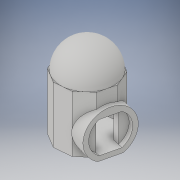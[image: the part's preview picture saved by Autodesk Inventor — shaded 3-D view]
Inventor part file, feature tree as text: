
AUTODESK INVENTOR PART (.ipt)
format: ipt  version: 2017 (Build 210142000, 142)  size: 312,320 bytes
history: native  units: in
note: dims shown in document units (in); Inventor stores cm internally (conversion verified against a paired STEP export)
features: sketch x8, extrude x7, other x4, mirror x1
ambient origin geometry x8: Origin, YZ Plane, XZ Plane, XY Plane, X Axis, Y Axis, Z Axis, Center Point
bodies: Solid1 (feature_tree)
feature tree (20):
  extrude  "bace"  Depth=1.0in TaperAngle=0.0deg
  extrude  "bace wall"  Depth=10.0in TaperAngle=0.0deg
  extrude  "bace cieiling"  Depth=6.6667in
  other  "dome work plane"
  other  "dome"
  extrude  "door frame"  Depth=6.6667in TaperAngle=0.0deg
  extrude  "corridor connection"  Depth=6.6667in
  extrude  "hide sliding doors"  Depth=4.6918in
  extrude  "left door slot"  TaperAngle=90.0deg  [1 undecoded]
  other  "door slot mirror"
  mirror  "Mirror1"
  other  "terminal connection parrale to door workplane"
  sketch  "Sketch1"  dims[d0=11.3835in d1=1.0in d2=0.0in]
  sketch  "Sketch2"  dims[d4=1.0in d5=10.0in d6=0.0in]
  sketch  "Sketch3"  dims[d8=1.0in d9=0.0in d14=6.6667in d15=4.0in]
  sketch  "Sketch7"  dims[d16=2.0in d17=6.6667in d18=1.6875in d19=0.0in]
  sketch  "Sketch8"  dims[d20=1.0in d21=0.0in d22=0.25in d23=0.5in d24=6.6667in]
  sketch  "Sketch9"  dims[d25=2.0in d26=0.0in d32=4.6918in]
  sketch  "Sketch10"  dims[d33=5.6918in d34=90.0deg]
  sketch  "Sketch11"  dims[d36=1.0in d37=1.0in d38=1.0in d42=1.2585in d43=0.0in]
note: 1 required parameter value undecoded (feature->parameter linkage not recoverable at this tier; creation-order binding heuristic only, values carry confidence <= 0.55)
